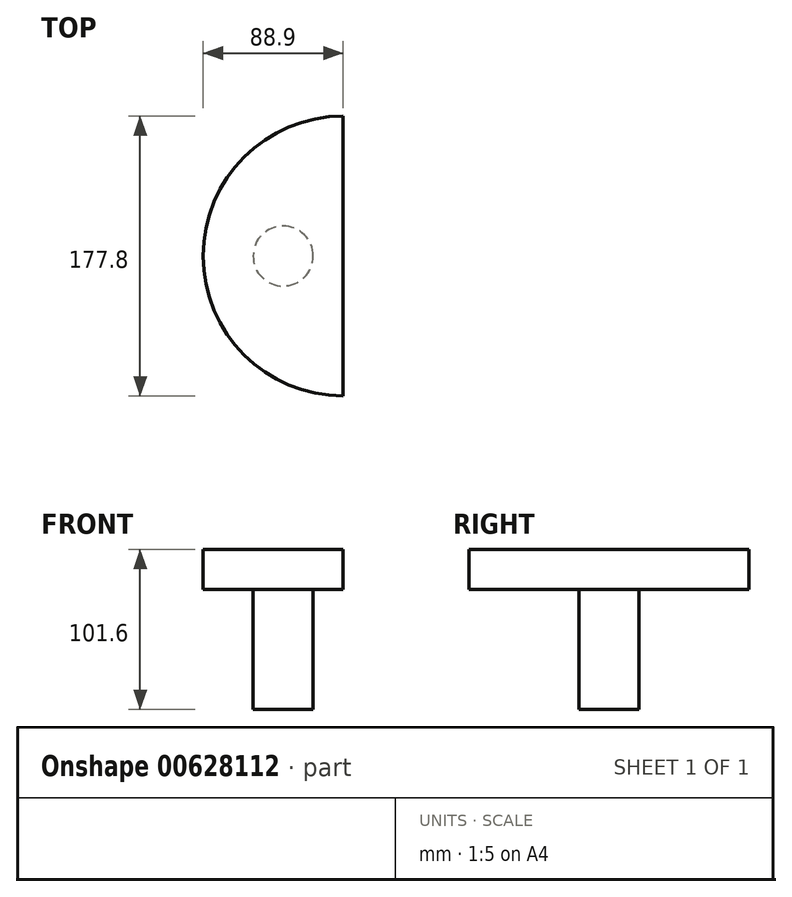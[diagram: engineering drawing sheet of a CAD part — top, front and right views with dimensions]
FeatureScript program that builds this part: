
annotation { "Feature Type Name" : "Feature", "Feature Type Description" : "" }
export const myFeature = defineFeature(function(context is Context, id is Id, definition is map)
    precondition{}
    {
        {
            var Q0;
            Q0=qCreatedBy(makeId("Top.planeOp"),FACE);
            var sketch = newSketch(context, id + "F0", { "sketchPlane" : qUnion([Q0])});
            skArc(sketch, "E0", {"start": v(0, 88.9) * mm, "mid": v(-88.9, 0) * mm, "end": v(0, -88.9) * mm});
            skLineSegment(sketch, "E1", {"start": v(0, 88.9) * mm, "end": v(0, -88.9) * mm});
            skSolve(sketch);
        }
        {
            var Q0;
            Q0=makeQuery(id+"F0.imprint","IMPRINT",FACE,{"disambiguationData":[TD([[makeQuery(id+"F0.imprint","IMPRINT",EDGE,{"derivedFrom":sQuery(id+"F0.wireOp",EDGE,"E0")}),1.0]])]});
            extrude(context, id + "F1", {"entities" : qUnion([Q0]), "depth" : 25.4 * mm, "offsetDistance" : 25.4 * mm});
        }
        {
            var Q0;
            Q0=makeQuery(id+"F1.opExtrude","CAP_FACE",FACE,{"disambiguationData":[OSD([sQuery(id+"F0.wireOp",EDGE,"E0"),sQuery(id+"F0.wireOp",EDGE,"E1")])],"isStart":true});
            var sketch = newSketch(context, id + "F2", { "sketchPlane" : qUnion([Q0])});
            skLineSegment(sketch, "E2", {"start": v(0, -2.67) * mm, "end": v(0, 0) * mm});
            skCircle(sketch, "E3", {"center": v(-38.1, 0) * mm, "radius": 19.05 * mm});
            skSolve(sketch);
        }
        {
            var Q0;
            Q0=makeQuery(id+"F2.imprint","IMPRINT",FACE,{"disambiguationData":[TD([[makeQuery(id+"F2.imprint","IMPRINT",EDGE,{"derivedFrom":sQuery(id+"F2.wireOp",EDGE,"E3")}),1.0]])]});
            extrude(context, id + "F3", {"entities" : qUnion([Q0]), "operationType" : NewBodyOperationType.ADD, "depth" : 76.2 * mm, "offsetDistance" : 25.4 * mm});
        }
    });
